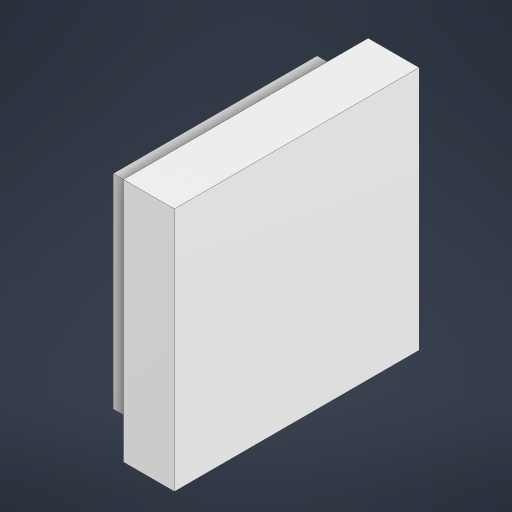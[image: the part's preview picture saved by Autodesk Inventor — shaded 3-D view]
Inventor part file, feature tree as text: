
AUTODESK INVENTOR PART (.ipt)
format: ipt  version: 2024.1 (Build 281209000, 209)  size: 160,768 bytes
history: native  units: mm
features: extrude x2, sketch x2
ambient origin geometry x8: Origin, YZ Plane, XZ Plane, XY Plane, X Axis, Y Axis, Z Axis, Center Point
bodies: Solid1 (feature_tree)
feature tree (4):
  extrude  "Extrusion1"  Depth=12.0mm
  extrude  "Extrusion2"  Depth=10.0mm
  sketch  "Sketch1"  dims[d0=12.0mm d1=12.0mm]
  sketch  "Sketch2"  dims[d2=2.5mm d3=0.0mm d4=10.0mm d5=10.0mm d6=1.5mm d7=0.0mm]
